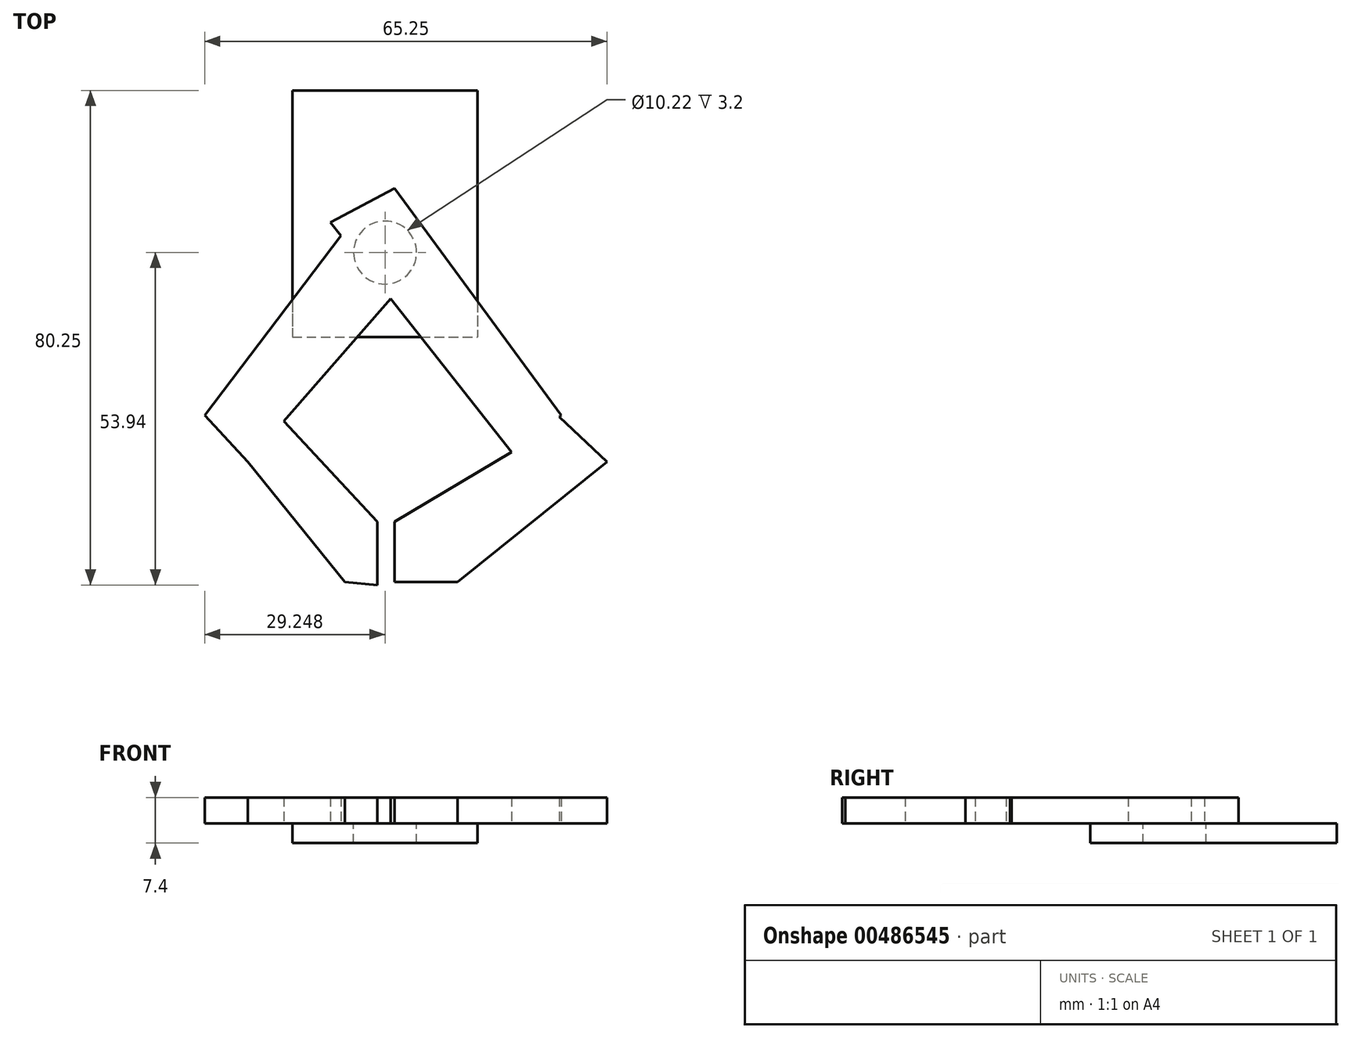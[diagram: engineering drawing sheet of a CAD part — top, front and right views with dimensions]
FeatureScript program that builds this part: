
annotation { "Feature Type Name" : "Feature", "Feature Type Description" : "" }
export const myFeature = defineFeature(function(context is Context, id is Id, definition is map)
    precondition{}
    {
        {
            var Q0;
            Q0=qCreatedBy(makeId("Top.planeOp"),FACE);
            var sketch = newSketch(context, id + "F0", { "sketchPlane" : qUnion([Q0])});
            skLineSegment(sketch, "E0.bottom", {"start": v(-58.62, 40) * mm, "end": v(-28.62, 40) * mm});
            skLineSegment(sketch, "E0.top", {"start": v(-58.62, 0) * mm, "end": v(-28.62, 0) * mm});
            skLineSegment(sketch, "E0.left", {"start": v(-58.62, 40) * mm, "end": v(-58.62, 0) * mm});
            skLineSegment(sketch, "E0.right", {"start": v(-28.62, 40) * mm, "end": v(-28.62, 0) * mm});
            skSolve(sketch);
        }
        {
            var Q0;
            Q0 = qSketchRegion(id + "F0", true);
            extrude(context, id + "F1", {"entities" : qUnion([Q0]), "depth" : 3.2 * mm, "offsetDistance" : 25 * mm});
        }
        {
            var Q0;
            Q0=makeQuery(id+"F1.opExtrude","CAP_FACE",FACE,{"disambiguationData":[OSD([sQuery(id+"F0.wireOp",EDGE,"E0.bottom"),sQuery(id+"F0.wireOp",EDGE,"E0.top"),sQuery(id+"F0.wireOp",EDGE,"E0.left"),sQuery(id+"F0.wireOp",EDGE,"E0.right")])],"isStart":false});
            var sketch = newSketch(context, id + "F2", { "sketchPlane" : qUnion([Q0])});
            skCircle(sketch, "E1", {"center": v(-43.62, 13.69) * mm, "radius": 5.11 * mm});
            skSolve(sketch);
        }
        {
            var Q0;
            Q0 = qSketchRegion(id + "F2", true);
            extrude(context, id + "F3", {"entities" : qUnion([Q0]), "operationType" : NewBodyOperationType.REMOVE, "oppositeDirection" : true, "depth" : 25 * mm, "offsetDistance" : 25 * mm});
        }
        {
            var Q0;
            Q0=makeQuery(id+"F1.opExtrude","CAP_FACE",FACE,{"disambiguationData":[OSD([sQuery(id+"F0.wireOp",EDGE,"E0.bottom"),sQuery(id+"F0.wireOp",EDGE,"E0.top"),sQuery(id+"F0.wireOp",EDGE,"E0.left"),sQuery(id+"F0.wireOp",EDGE,"E0.right")])],"isStart":false});
            var sketch = newSketch(context, id + "F4", { "sketchPlane" : qUnion([Q0])});
            skLineSegment(sketch, "E2", {"start": v(-47.87, 20.25) * mm, "end": v(-72.87, -12.75) * mm});
            skLineSegment(sketch, "E3", {"start": v(-35.62, 14.25) * mm, "end": v(-65.87, -20.25) * mm});
            skLineSegment(sketch, "E4", {"start": v(-47.87, 20.25) * mm, "end": v(-35.62, 14.25) * mm});
            skLineSegment(sketch, "E5", {"start": v(-72.87, -12.75) * mm, "end": v(-65.87, -20.25) * mm});
            skLineSegment(sketch, "E6", {"start": v(-67.5, -5.66) * mm, "end": v(-44.87, -30) * mm});
            skLineSegment(sketch, "E7", {"start": v(-65.87, -20.25) * mm, "end": v(-50.12, -39.75) * mm});
            skLineSegment(sketch, "E8", {"start": v(-44.87, -30) * mm, "end": v(-44.87, -40.25) * mm});
            skLineSegment(sketch, "E9", {"start": v(-50.12, -39.75) * mm, "end": v(-44.87, -40.25) * mm});
            skLineSegment(sketch, "E10", {"start": v(-52.5, 18.58) * mm, "end": v(-42.09, 24.08) * mm});
            skLineSegment(sketch, "E11", {"start": v(-42.09, 24.08) * mm, "end": v(-15.04, -12.75) * mm});
            skLineSegment(sketch, "E12", {"start": v(-15.04, -12.75) * mm, "end": v(-23.08, -18.67) * mm});
            skLineSegment(sketch, "E13", {"start": v(-23.08, -18.67) * mm, "end": v(-52.5, 18.58) * mm});
            skLineSegment(sketch, "E14", {"start": v(-23.08, -18.67) * mm, "end": v(-42.09, -30) * mm});
            skLineSegment(sketch, "E15", {"start": v(-42.09, -30) * mm, "end": v(-42.09, -39.75) * mm});
            skLineSegment(sketch, "E16", {"start": v(-42.09, -39.75) * mm, "end": v(-31.87, -39.75) * mm});
            skLineSegment(sketch, "E17", {"start": v(-31.87, -39.75) * mm, "end": v(-7.62, -20.25) * mm});
            skLineSegment(sketch, "E18", {"start": v(-7.62, -20.25) * mm, "end": v(-15.87, -12.5) * mm});
            skSolve(sketch);
        }
        {
            var Q0;
            Q0 = qSketchRegion(id + "F4", true);
            extrude(context, id + "F5", {"entities" : qUnion([Q0]), "operationType" : NewBodyOperationType.ADD, "depth" : 4.2 * mm, "offsetDistance" : 25 * mm});
        }
    });
